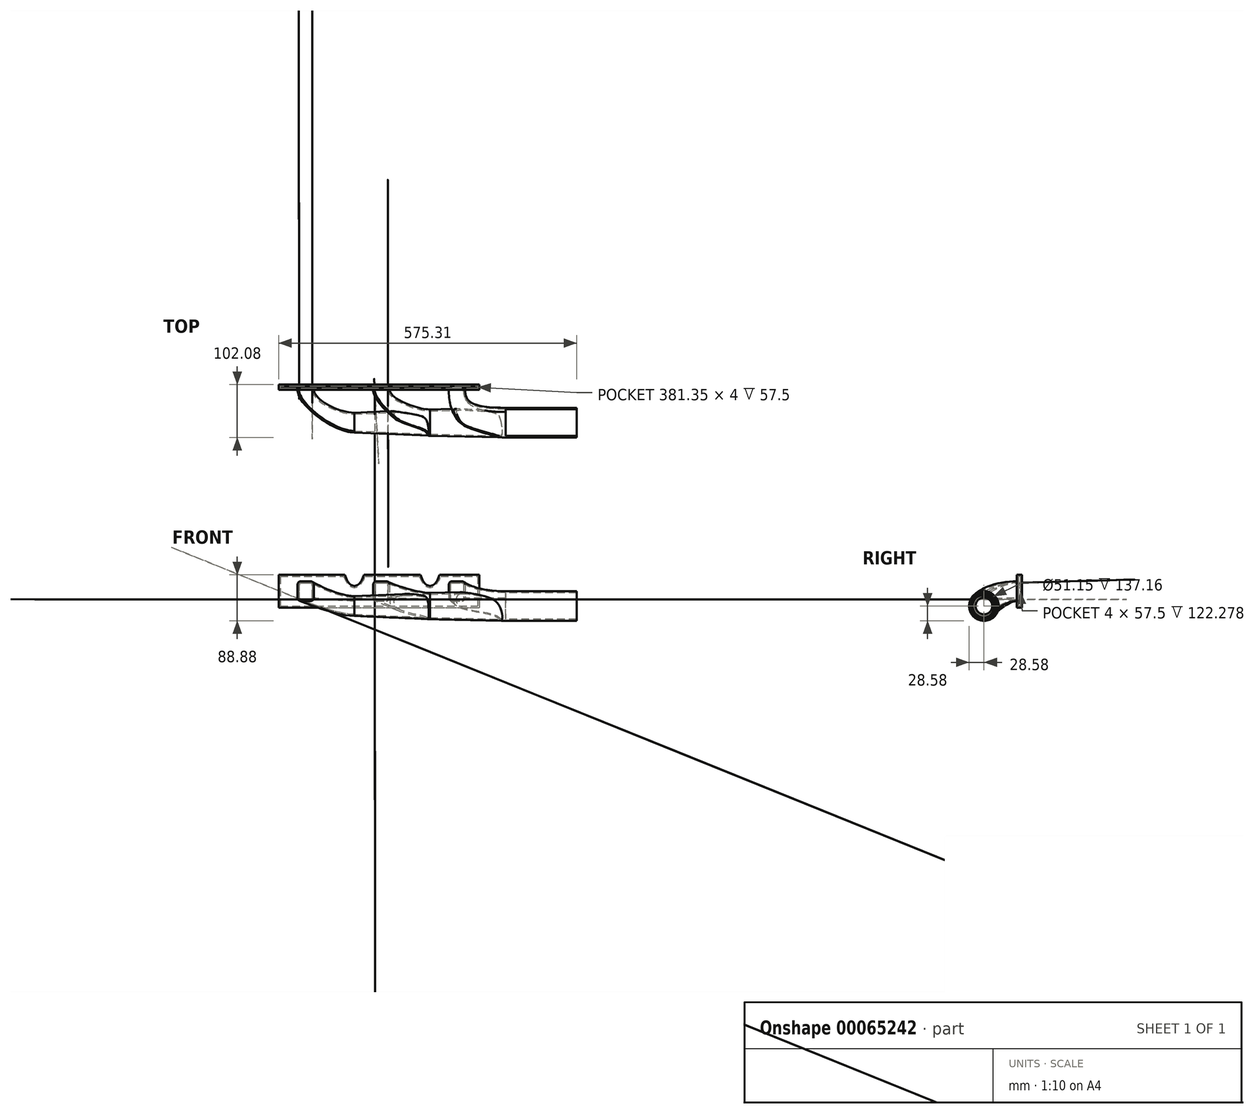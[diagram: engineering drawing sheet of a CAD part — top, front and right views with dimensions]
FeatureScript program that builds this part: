
annotation { "Feature Type Name" : "Feature", "Feature Type Description" : "" }
export const myFeature = defineFeature(function(context is Context, id is Id, definition is map)
    precondition{}
    {
        {
            var Q0;
            Q0=qCreatedBy(makeId("Front.planeOp"),FACE);
            var sketch = newSketch(context, id + "F0", { "sketchPlane" : qUnion([Q0])});
            skLineSegment(sketch, "E0.bottom", {"start": v(-146.05, 0) * mm, "end": v(-18.63, 0) * mm});
            skLineSegment(sketch, "E0.left", {"start": v(-146.05, 0) * mm, "end": v(-146.05, -63.5) * mm});
            skLineSegment(sketch, "E0.right", {"start": v(241.3, 0) * mm, "end": v(241.3, -63.5) * mm});
            skLineSegment(sketch, "E1", {"start": v(-146.05, -31.75) * mm, "end": v(241.3, -31.75) * mm, "construction": true});
            skEllipticalArc(sketch, "E2.MirrorCS", {});
            skEllipticalArc(sketch, "E3.MirrorCS", {});
            skLineSegment(sketch, "E4", {"start": v(-146.05, -63.5) * mm, "end": v(241.3, -63.5) * mm});
            skLineSegment(sketch, "E5.trimOffspring", {"start": v(18.63, 0) * mm, "end": v(127.42, 0) * mm});
            skLineSegment(sketch, "E6.trimOffspring", {"start": v(164.68, 0) * mm, "end": v(241.3, 0) * mm});
            const initialGuessF0  = {"E2.MirrorCS": [0, 0.03568, 0, -1, 0.05734, 0.023805, 5.3840067622967815, 0.8991785448828047], "E3.MirrorCS": [0.14605, 0.03568, 0, -1, 0.05734, 0.023805, 5.3840067622967815, 0.8991785448828047]};
            skSetInitialGuess(sketch, initialGuessF0);
            skSolve(sketch);
        }
        {
            var Q0;
            Q0=qCreatedBy(makeId("Right.planeOp"),FACE);
            cPlane(context, id + "F1", {"entities" : qUnion([Q0]), "cplaneType" : CPlaneType.OFFSET, "offset" : 146.05 * mm, "width" : 152.4 * mm, "height" : 152.4 * mm});
        }
        {
            var Q0;
            Q0=qCreatedBy(id+"F1.planeOp",FACE);
            cPlane(context, id + "F2", {"entities" : qUnion([Q0]), "cplaneType" : CPlaneType.OFFSET, "offset" : 146.05 * mm, "width" : 152.4 * mm, "height" : 152.4 * mm});
        }
        {
            var Q0;
            Q0=qCreatedBy(makeId("Front.planeOp"),FACE);
            var sketch = newSketch(context, id + "F3", { "sketchPlane" : qUnion([Q0])});
            skLineSegment(sketch, "E7.rect.bottom", {"start": v(-103.5, -12.7) * mm, "end": v(-84.45, -12.7) * mm});
            skArc(sketch, "E8.filletArc", {"start": v(-78.1, -19.05) * mm, "mid": v(-79.96, -14.56) * mm, "end": v(-84.45, -12.7) * mm});
            skLineSegment(sketch, "E7.rect.right", {"start": v(-78.1, -19.05) * mm, "end": v(-78.1, -44.45) * mm});
            skArc(sketch, "E9.filletArc", {"start": v(-84.45, -50.8) * mm, "mid": v(-79.96, -48.94) * mm, "end": v(-78.1, -44.45) * mm});
            skLineSegment(sketch, "E7.rect.top", {"start": v(-103.5, -50.8) * mm, "end": v(-84.45, -50.8) * mm});
            skArc(sketch, "E10.filletArc", {"start": v(-109.86, -44.45) * mm, "mid": v(-108, -48.94) * mm, "end": v(-103.5, -50.8) * mm});
            skLineSegment(sketch, "E7.rect.left", {"start": v(-109.86, -19.05) * mm, "end": v(-109.86, -44.45) * mm});
            skArc(sketch, "E11.filletArc", {"start": v(-103.5, -12.7) * mm, "mid": v(-108, -14.56) * mm, "end": v(-109.86, -19.05) * mm});
            skLineSegment(sketch, "E12", {"start": v(-137.86, -31.75) * mm, "end": v(-109.86, -31.75) * mm, "construction": true});
            skPoint(sketch, "E12.startSnap0", {"position": v(-109.86, -31.75) * mm});
            skSolve(sketch);
        }
        {
            var Q0;
            Q0=qCreatedBy(makeId("Front.planeOp"),FACE);
            var sketch = newSketch(context, id + "F4", { "sketchPlane" : qUnion([Q0])});
            skLineSegment(sketch, "E13.rect.bottom", {"start": v(42.55, -12.7) * mm, "end": v(61.6, -12.7) * mm});
            skArc(sketch, "E14.filletArc", {"start": v(67.95, -19.05) * mm, "mid": v(66.09, -14.56) * mm, "end": v(61.6, -12.7) * mm});
            skLineSegment(sketch, "E13.rect.right", {"start": v(67.95, -19.05) * mm, "end": v(67.95, -44.45) * mm});
            skArc(sketch, "E15.filletArc", {"start": v(61.6, -50.8) * mm, "mid": v(66.09, -48.94) * mm, "end": v(67.95, -44.45) * mm});
            skLineSegment(sketch, "E13.rect.top", {"start": v(42.55, -50.8) * mm, "end": v(61.6, -50.8) * mm});
            skArc(sketch, "E16.filletArc", {"start": v(36.2, -44.45) * mm, "mid": v(38.05, -48.94) * mm, "end": v(42.55, -50.8) * mm});
            skLineSegment(sketch, "E13.rect.left", {"start": v(36.2, -19.05) * mm, "end": v(36.2, -44.45) * mm});
            skArc(sketch, "E17.filletArc", {"start": v(42.55, -12.7) * mm, "mid": v(38.05, -14.56) * mm, "end": v(36.2, -19.05) * mm});
            skLineSegment(sketch, "E18", {"start": v(36.2, -31.75) * mm, "end": v(-146.05, -31.75) * mm, "construction": true});
            skSolve(sketch);
        }
        {
            var Q0;
            Q0=qCreatedBy(makeId("Front.planeOp"),FACE);
            var sketch = newSketch(context, id + "F5", { "sketchPlane" : qUnion([Q0])});
            skLineSegment(sketch, "E19.rect.bottom", {"start": v(188.6, -12.7) * mm, "end": v(207.65, -12.7) * mm});
            skArc(sketch, "E20.filletArc", {"start": v(214, -19.05) * mm, "mid": v(212.14, -14.56) * mm, "end": v(207.65, -12.7) * mm});
            skLineSegment(sketch, "E19.rect.right", {"start": v(214, -19.05) * mm, "end": v(214, -44.45) * mm});
            skArc(sketch, "E21.filletArc", {"start": v(207.65, -50.8) * mm, "mid": v(212.14, -48.94) * mm, "end": v(214, -44.45) * mm});
            skLineSegment(sketch, "E19.rect.top", {"start": v(188.6, -50.8) * mm, "end": v(207.65, -50.8) * mm});
            skArc(sketch, "E22.filletArc", {"start": v(182.25, -44.45) * mm, "mid": v(184.1, -48.94) * mm, "end": v(188.6, -50.8) * mm});
            skLineSegment(sketch, "E19.rect.left", {"start": v(182.25, -19.05) * mm, "end": v(182.25, -44.45) * mm});
            skArc(sketch, "E23.filletArc", {"start": v(188.6, -12.7) * mm, "mid": v(184.1, -14.56) * mm, "end": v(182.25, -19.05) * mm});
            skLineSegment(sketch, "E24", {"start": v(182.25, -31.75) * mm, "end": v(-146.05, -31.75) * mm, "construction": true});
            skSolve(sketch);
        }
        {
            var Q0;
            Q0=qCreatedBy(makeId("Right.planeOp"),FACE);
            var sketch = newSketch(context, id + "F6", { "sketchPlane" : qUnion([Q0])});
            skCircle(sketch, "E25", {"center": v(-63.5, -60.3) * mm, "radius": 19.05 * mm});
            skSolve(sketch);
        }
        {
            var Q0;
            Q0=qCreatedBy(id+"F2.planeOp",FACE);
            var sketch = newSketch(context, id + "F7", { "sketchPlane" : qUnion([Q0])});
            skCircle(sketch, "E26", {"center": v(-63.5, -60.3) * mm, "radius": 28.57 * mm});
            skSolve(sketch);
        }
        {
            var Q0;
            Q0=qCreatedBy(id+"F1.planeOp",FACE);
            var sketch = newSketch(context, id + "F8", { "sketchPlane" : qUnion([Q0])});
            skCircle(sketch, "E27", {"center": v(-63.5, -60.3) * mm, "radius": 25.4 * mm});
            skSolve(sketch);
        }
        {
            var Q0;
            Q0=makeQuery(id+"F6.imprint","IMPRINT",FACE,{"disambiguationData":[TD([[makeQuery(id+"F6.imprint","IMPRINT",EDGE,{"derivedFrom":sQuery(id+"F6.wireOp",EDGE,"E25")}),1.0]])]});
            var Q1;
            Q1=makeQuery(id+"F8.imprint","IMPRINT",FACE,{"disambiguationData":[TD([[makeQuery(id+"F8.imprint","IMPRINT",EDGE,{"derivedFrom":sQuery(id+"F8.wireOp",EDGE,"E27")}),1.0]])]});
            loft(context, id + "F9", {"sheetProfilesArray" : [{ "sheetProfileEntities" : qUnion([Q0]) }, { "sheetProfileEntities" : qUnion([Q1]) }]});
        }
        {
            var Q1;
            Q1 = qSketchRegion(id + "F7", true);
            var Q2;
            Q2 = qSketchRegion(id + "F8", true);
            loft(context, id + "F10", {"operationType" : NewBodyOperationType.ADD, "sheetProfilesArray" : [{ "sheetProfileEntities" : qUnion([Q1]) }, { "sheetProfileEntities" : qUnion([Q2]) }]});
        }
        {
            var Q1;
            Q1 = qSketchRegion(id + "F6", true);
            var Q2;
            Q2 = qSketchRegion(id + "F3", true);
            loft(context, id + "F11", {"operationType" : NewBodyOperationType.ADD, "startCondition" : LoftEndDerivativeType.NORMAL_TO_PROFILE, "startMagnitude" : 1.1, "endCondition" : LoftEndDerivativeType.NORMAL_TO_PROFILE, "endMagnitude" : 1.1, "sheetProfilesArray" : [{ "sheetProfileEntities" : qUnion([Q1]) }, { "sheetProfileEntities" : qUnion([Q2]) }]});
        }
        {
            var Q1;
            Q1 = qSketchRegion(id + "F7", true);
            var Q2;
            Q2 = qSketchRegion(id + "F5", true);
            loft(context, id + "F12", {"operationType" : NewBodyOperationType.ADD, "startCondition" : LoftEndDerivativeType.NORMAL_TO_PROFILE, "startMagnitude" : 2, "endCondition" : LoftEndDerivativeType.NORMAL_TO_PROFILE, "endMagnitude" : 2, "sheetProfilesArray" : [{ "sheetProfileEntities" : qUnion([Q1]) }, { "sheetProfileEntities" : qUnion([Q2]) }]});
        }
        {
            var Q1;
            Q1 = qSketchRegion(id + "F8", true);
            var Q2;
            Q2 = qSketchRegion(id + "F4", true);
            loft(context, id + "F13", {"operationType" : NewBodyOperationType.ADD, "startCondition" : LoftEndDerivativeType.NORMAL_TO_PROFILE, "startMagnitude" : 1, "endCondition" : LoftEndDerivativeType.NORMAL_TO_PROFILE, "endMagnitude" : 1, "sheetProfilesArray" : [{ "sheetProfileEntities" : qUnion([Q1]) }, { "sheetProfileEntities" : qUnion([Q2]) }]});
        }
        {
            var Q0;
            Q0 = qSketchRegion(id + "F0", true);
            extrude(context, id + "F14", {"entities" : qUnion([Q0]), "operationType" : NewBodyOperationType.ADD, "oppositeDirection" : true, "depth" : 10 * mm});
        }
        {
            var Q0;
            Q0=makeQuery(id+"F7.imprint","IMPRINT",FACE,{"disambiguationData":[TD([[makeQuery(id+"F7.imprint","IMPRINT",EDGE,{"derivedFrom":sQuery(id+"F7.wireOp",EDGE,"E26")}),1.0]])]});
            var sketch = newSketch(context, id + "F15", { "sketchPlane" : qUnion([Q0])});
            skCircle(sketch, "E28", {"center": v(-63.5, -60.3) * mm, "radius": 28.57 * mm});
            skSolve(sketch);
        }
        {
            var Q0;
            Q0 = qSketchRegion(id + "F15", true);
            extrude(context, id + "F16", {"entities" : qUnion([Q0]), "operationType" : NewBodyOperationType.ADD, "depth" : 137.16 * mm});
        }
        {
            var Q0;
            Q0=makeQuery(id+"F16.opExtrude","CAP_FACE",FACE,{"disambiguationData":[OSD([sQuery(id+"F15.wireOp",EDGE,"E28")])],"isStart":false});
            var Q1;
            Q1=makeQuery(id+"F16.opExtrude","CAP_FACE",FACE,{"disambiguationData":[OSD([sQuery(id+"F15.wireOp",EDGE,"E28")])],"isStart":false});
            shell(context, id + "F17", {"entities" : qUnion([Q0, Q1]), "thickness" : 3 * mm});
        }
    });
